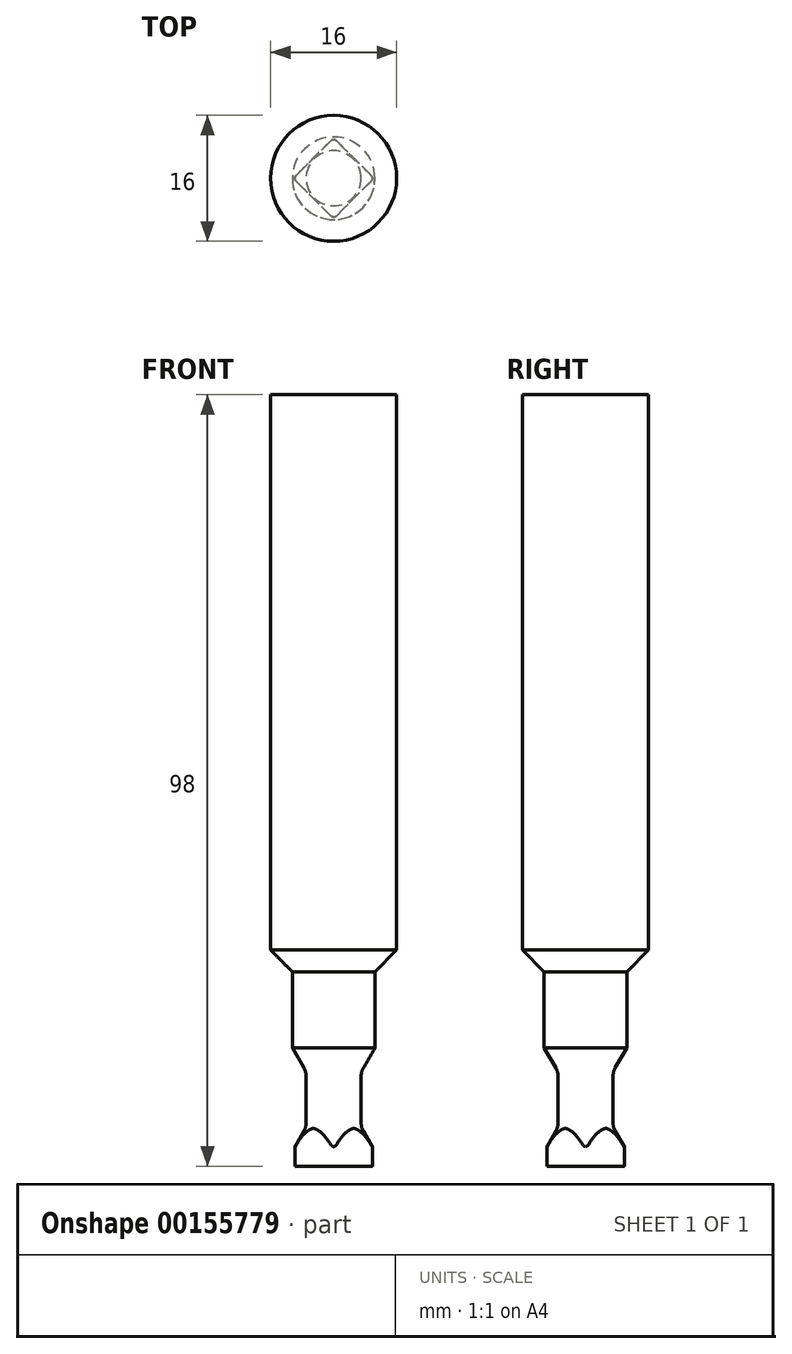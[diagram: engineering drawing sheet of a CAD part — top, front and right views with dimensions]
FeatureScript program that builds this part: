
annotation { "Feature Type Name" : "Feature", "Feature Type Description" : "" }
export const myFeature = defineFeature(function(context is Context, id is Id, definition is map)
    precondition{}
    {
        {
            var Q0;
            Q0=qCreatedBy(makeId("Front.planeOp"),FACE);
            var sketch = newSketch(context, id + "F0", { "sketchPlane" : qUnion([Q0])});
            skLineSegment(sketch, "E0", {"start": v(0, 0) * mm, "end": v(-5.2, 0) * mm});
            skLineSegment(sketch, "E1", {"start": v(-5.2, 0) * mm, "end": v(-5.2, 2) * mm});
            skLineSegment(sketch, "E2", {"start": v(-5.2, 2) * mm, "end": v(-3.5, 4.94) * mm});
            skLineSegment(sketch, "E3", {"start": v(-3.5, 4.94) * mm, "end": v(-3.5, 12) * mm});
            skLineSegment(sketch, "E4", {"start": v(-3.5, 12) * mm, "end": v(-5.25, 15.03) * mm});
            skLineSegment(sketch, "E5", {"start": v(-5.25, 15.03) * mm, "end": v(-5.25, 24.7) * mm});
            skLineSegment(sketch, "E6", {"start": v(-5.25, 24.7) * mm, "end": v(-8, 27.45) * mm});
            skLineSegment(sketch, "E7", {"start": v(-8, 27.45) * mm, "end": v(-8, 98) * mm});
            skLineSegment(sketch, "E8", {"start": v(-8, 98) * mm, "end": v(0, 98) * mm});
            skLineSegment(sketch, "E9", {"start": v(0, 98) * mm, "end": v(0, 0) * mm});
            skLineSegment(sketch, "E10", {"start": v(0, -12.18) * mm, "end": v(0, 66) * mm, "construction": true});
            skSolve(sketch);
        }
        {
            var Q0;
            Q0=makeQuery(id+"F0.imprint","IMPRINT",FACE,{"disambiguationData":[TD([[makeQuery(id+"F0.imprint","IMPRINT",EDGE,{"derivedFrom":sQuery(id+"F0.wireOp",EDGE,"E0")}),-1.0]])]});
            var Q1;
            Q1=sQuery(id+"F0.wireOp",EDGE,"E10");
            revolve(context, id + "F1", {"entities" : qUnion([Q0]), "axis" : qUnion([Q1]), "revolveType" : RevolveType.FULL});
        }
        {
            var Q0;
            Q0=makeQuery(id+"F1.opRevolve","SWEPT_EDGE",EDGE,{"disambiguationData":[OSD([sQuery(id+"F0.wireOp",EDGE,"E2"),sQuery(id+"F0.wireOp",EDGE,"E3")])]});
            var Q1;
            Q1=makeQuery(id+"F1.opRevolve","SWEPT_EDGE",EDGE,{"disambiguationData":[OSD([sQuery(id+"F0.wireOp",EDGE,"E3"),sQuery(id+"F0.wireOp",EDGE,"E4")])]});
            fillet(context, id + "F2", {"entities" : qUnion([Q0, Q1]), "radius" : 2 * mm, "tangentPropagation" : true, "allowEdgeOverflow" : false});
        }
        {
            var Q0;
            Q0=qCreatedBy(makeId("Top.planeOp"),FACE);
            var sketch = newSketch(context, id + "F3", { "sketchPlane" : qUnion([Q0])});
            skLineSegment(sketch, "E11", {"start": v(0, -15.4) * mm, "end": v(0, 14.8) * mm, "construction": true});
            skLineSegment(sketch, "E12", {"start": v(-13.99, 0) * mm, "end": v(13.86, 0) * mm, "construction": true});
            skLineSegment(sketch, "E13", {"start": v(-4.77, -0.35) * mm, "end": v(-0.35, -4.77) * mm});
            skLineSegment(sketch, "E14.MirrorCS", {"start": v(0.35, 4.77) * mm, "end": v(4.77, 0.35) * mm});
            skLineSegment(sketch, "E15", {"start": v(-4.77, 0.35) * mm, "end": v(-0.35, 4.77) * mm});
            skLineSegment(sketch, "E16", {"start": v(0.35, -4.77) * mm, "end": v(4.77, -0.35) * mm});
            skPoint(sketch, "E17.visualSharp", {"position": v(-3.78, -3.78) * mm});
            skArc(sketch, "E17.filletArc", {"start": v(-4.77, 0.35) * mm, "mid": v(-4.92, 0) * mm, "end": v(-4.77, -0.35) * mm});
            skPoint(sketch, "E18.visualSharp", {"position": v(3.77, -3.78) * mm});
            skArc(sketch, "E18.filletArc", {"start": v(-0.35, -4.77) * mm, "mid": v(0, -4.92) * mm, "end": v(0.35, -4.77) * mm});
            skPoint(sketch, "E19.visualSharp", {"position": v(3.78, 3.78) * mm});
            skArc(sketch, "E19.filletArc", {"start": v(4.77, -0.35) * mm, "mid": v(4.92, 0) * mm, "end": v(4.77, 0.35) * mm});
            skPoint(sketch, "E20.visualSharp", {"position": v(-3.78, 3.78) * mm});
            skArc(sketch, "E20.filletArc", {"start": v(0.35, 4.77) * mm, "mid": v(0, 4.92) * mm, "end": v(-0.35, 4.77) * mm});
            skCircle(sketch, "E21.0", {"center": v(0, 0) * mm, "radius": 5.2 * mm});
            skSolve(sketch);
        }
        {
            var Q0;
            Q0=makeQuery(id+"F3.imprint","IMPRINT",FACE,{"disambiguationData":[TD([[makeQuery(id+"F3.imprint","IMPRINT",EDGE,{"derivedFrom":sQuery(id+"F3.wireOp",EDGE,"E13")}),-1.0]])]});
            var Q1;
            Q1=makeQuery(id+"F2.opFillet","BLEND_FACE",FACE,{"disambiguationData":[OSD([sQuery(id+"F0.wireOp",EDGE,"E2"),sQuery(id+"F0.wireOp",EDGE,"E3")])]});
            extrude(context, id + "F4", {"entities" : qUnion([Q0]), "operationType" : NewBodyOperationType.REMOVE, "endBound" : BoundingType.UP_TO_SURFACE, "endBoundEntityFace" : qUnion([Q1]), "depth" : 25 * mm});
        }
    });
